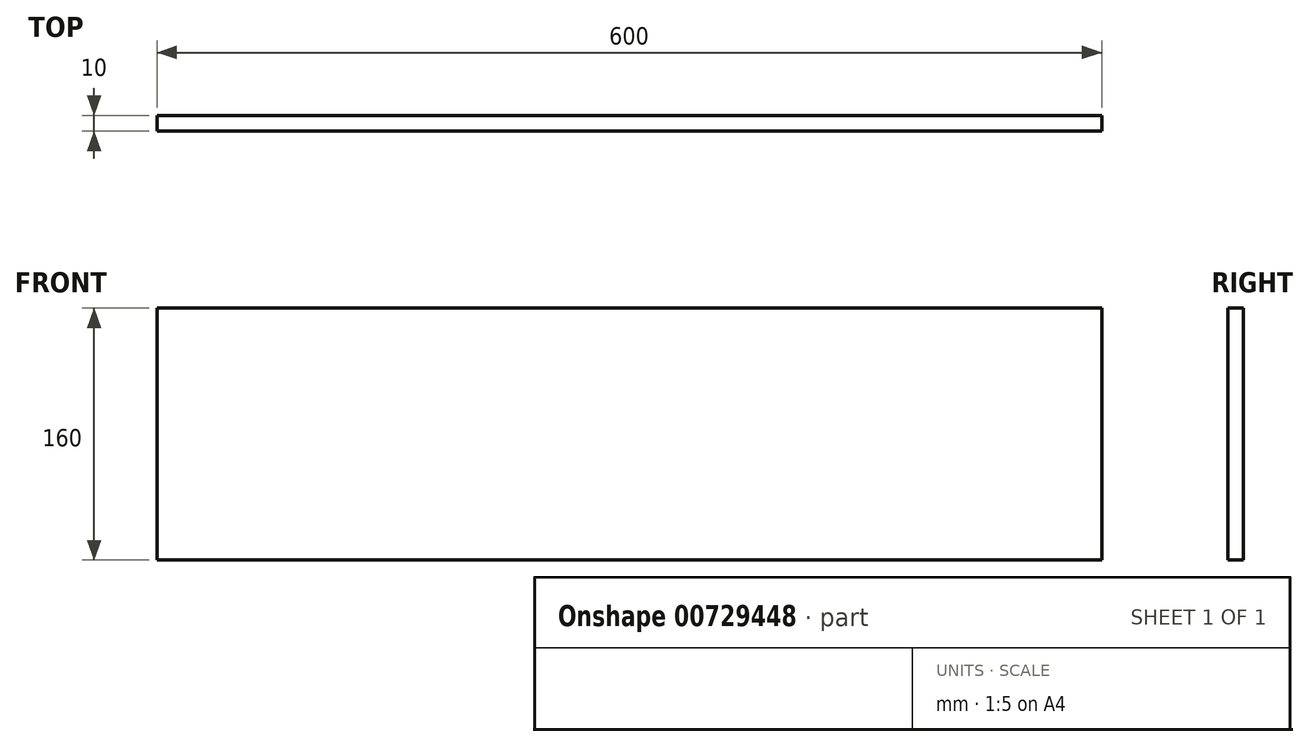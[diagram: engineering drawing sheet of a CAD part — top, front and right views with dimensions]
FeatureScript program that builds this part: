
annotation { "Feature Type Name" : "Feature", "Feature Type Description" : "" }
export const myFeature = defineFeature(function(context is Context, id is Id, definition is map)
    precondition{}
    {
        {
            var Q0;
            Q0=qCreatedBy(makeId("Front.planeOp"),FACE);
            var sketch = newSketch(context, id + "F0", { "sketchPlane" : qUnion([Q0])});
            skLineSegment(sketch, "E0.bottom", {"start": v(-300, 80) * mm, "end": v(300, 80) * mm});
            skLineSegment(sketch, "E0.top", {"start": v(-300, -80) * mm, "end": v(300, -80) * mm});
            skLineSegment(sketch, "E0.left", {"start": v(-300, 80) * mm, "end": v(-300, -80) * mm});
            skLineSegment(sketch, "E0.right", {"start": v(300, 80) * mm, "end": v(300, -80) * mm});
            skPoint(sketch, "E0.middle", {"position": v(0, 0) * mm});
            skSolve(sketch);
        }
        {
            var Q0;
            Q0=makeQuery(id+"F0.imprint","IMPRINT",FACE,{"disambiguationData":[TD([[makeQuery(id+"F0.imprint","IMPRINT",EDGE,{"derivedFrom":sQuery(id+"F0.wireOp",EDGE,"E0.bottom")}),-1.0]])]});
            extrude(context, id + "F1", {"entities" : qUnion([Q0]), "depth" : 10 * mm, "offsetDistance" : 25 * mm});
        }
    });
